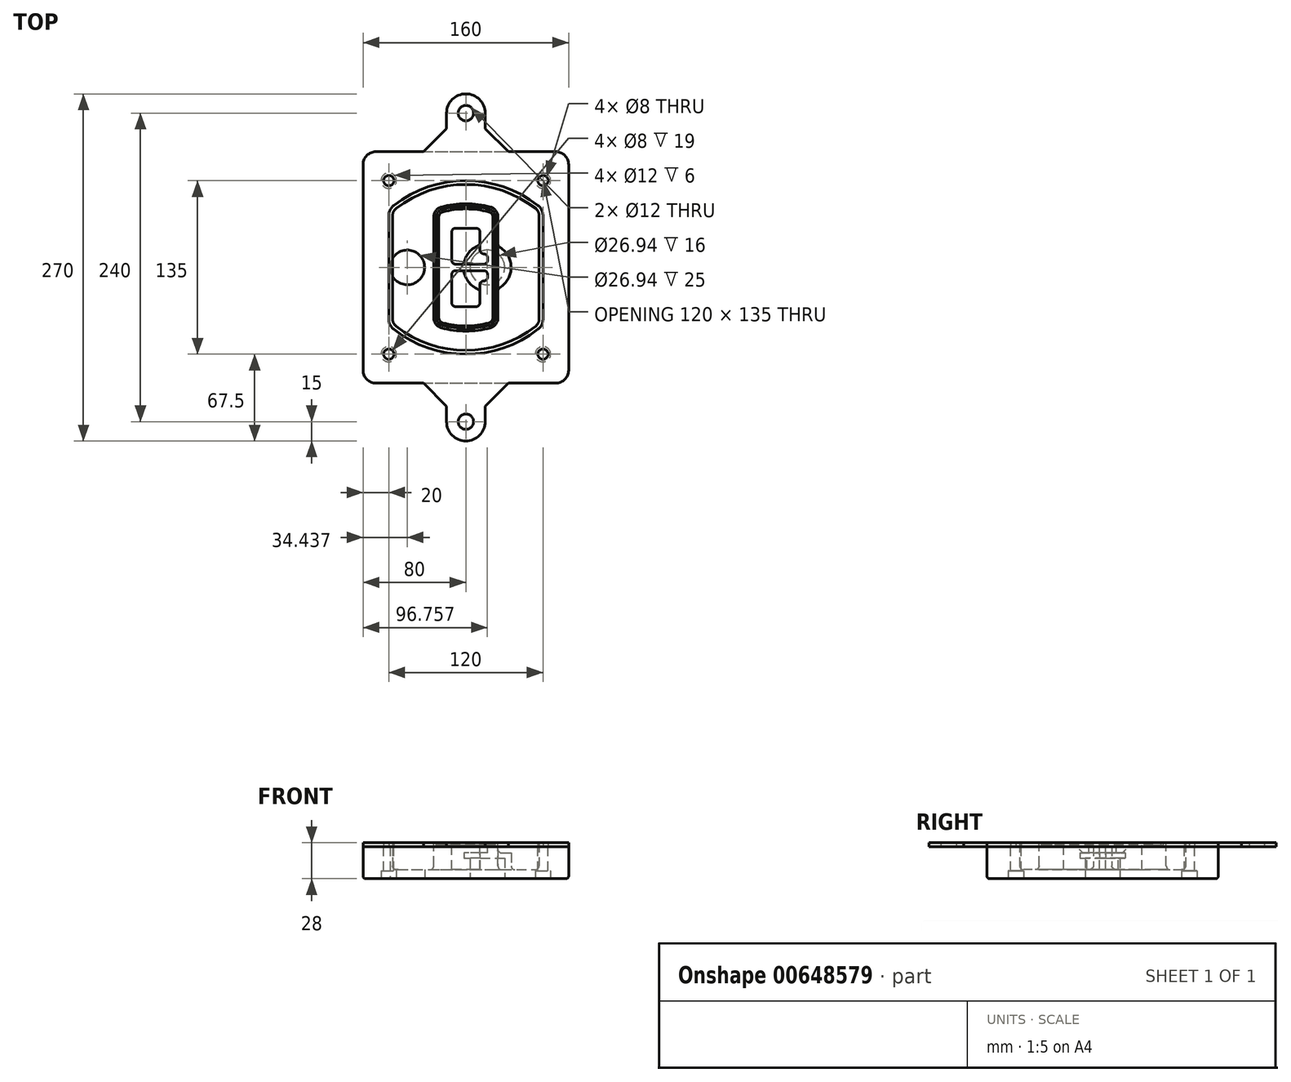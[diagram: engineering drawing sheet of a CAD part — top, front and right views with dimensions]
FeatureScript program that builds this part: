
annotation { "Feature Type Name" : "Feature", "Feature Type Description" : "" }
export const myFeature = defineFeature(function(context is Context, id is Id, definition is map)
    precondition{}
    {
        {
            var Q0;
            Q0=qCreatedBy(makeId("Top.planeOp"),FACE);
            var sketch = newSketch(context, id + "F0", { "sketchPlane" : qUnion([Q0])});
            skPoint(sketch, "E0.rect.middle", {"position": v(0, 0) * mm});
            skLineSegment(sketch, "E1.bottom", {"start": v(-70, -90) * mm, "end": v(70, -90) * mm});
            skLineSegment(sketch, "E1.top", {"start": v(-70, 90) * mm, "end": v(70, 90) * mm});
            skLineSegment(sketch, "E1.left", {"start": v(-80, -80) * mm, "end": v(-80, 80) * mm});
            skLineSegment(sketch, "E1.right", {"start": v(80, -80) * mm, "end": v(80, 80) * mm});
            skLineSegment(sketch, "E2", {"start": v(-80, 90) * mm, "end": v(80, -90) * mm, "construction": true});
            skLineSegment(sketch, "E3", {"start": v(80, 90) * mm, "end": v(-80, -90) * mm, "construction": true});
            skCircle(sketch, "E4", {"center": v(-60, 67.5) * mm, "radius": 4 * mm});
            skCircle(sketch, "E5", {"center": v(60, 67.5) * mm, "radius": 4 * mm});
            skCircle(sketch, "E6", {"center": v(60, -67.5) * mm, "radius": 4 * mm});
            skCircle(sketch, "E7", {"center": v(-60, -67.5) * mm, "radius": 4 * mm});
            skLineSegment(sketch, "E8", {"start": v(-60, 67.5) * mm, "end": v(60, 67.5) * mm, "construction": true});
            skLineSegment(sketch, "E9", {"start": v(60, 67.5) * mm, "end": v(60, -67.5) * mm, "construction": true});
            skLineSegment(sketch, "E10", {"start": v(60, -67.5) * mm, "end": v(-60, -67.5) * mm, "construction": true});
            skLineSegment(sketch, "E11", {"start": v(-60, -67.5) * mm, "end": v(-60, 67.5) * mm, "construction": true});
            skLineSegment(sketch, "E12", {"start": v(-60, 40.3) * mm, "end": v(-60, -40.3) * mm});
            skLineSegment(sketch, "E13", {"start": v(60, 40.3) * mm, "end": v(60, -40.3) * mm});
            skArc(sketch, "E14", {"start": v(56.15, 48.18) * mm, "mid": v(0, 67.5) * mm, "end": v(-56.15, 48.18) * mm});
            skArc(sketch, "E15", {"start": v(-56.15, -48.18) * mm, "mid": v(0, -67.5) * mm, "end": v(56.15, -48.18) * mm});
            skLineSegment(sketch, "E16", {"start": v(-60, 0) * mm, "end": v(60, 0) * mm, "construction": true});
            skPoint(sketch, "E17.visualSharp", {"position": v(-60, -45) * mm});
            skArc(sketch, "E17.filletArc", {"start": v(-60, -40.3) * mm, "mid": v(-58.99, -44.68) * mm, "end": v(-56.15, -48.18) * mm});
            skPoint(sketch, "E18.visualSharp", {"position": v(-60, 45) * mm});
            skArc(sketch, "E18.filletArc", {"start": v(-56.15, 48.18) * mm, "mid": v(-58.99, 44.68) * mm, "end": v(-60, 40.3) * mm});
            skPoint(sketch, "E19.visualSharp", {"position": v(60, 45) * mm});
            skArc(sketch, "E19.filletArc", {"start": v(60, 40.3) * mm, "mid": v(58.99, 44.68) * mm, "end": v(56.15, 48.18) * mm});
            skPoint(sketch, "E20.visualSharp", {"position": v(60, -45) * mm});
            skArc(sketch, "E20.filletArc", {"start": v(56.15, -48.18) * mm, "mid": v(58.99, -44.68) * mm, "end": v(60, -40.3) * mm});
            skPoint(sketch, "E21.visualSharp", {"position": v(-80, 90) * mm});
            skArc(sketch, "E21.filletArc", {"start": v(-70, 90) * mm, "mid": v(-77.07, 87.07) * mm, "end": v(-80, 80) * mm});
            skPoint(sketch, "E22.visualSharp", {"position": v(80, 90) * mm});
            skArc(sketch, "E22.filletArc", {"start": v(80, 80) * mm, "mid": v(77.07, 87.07) * mm, "end": v(70, 90) * mm});
            skPoint(sketch, "E23.visualSharp", {"position": v(80, -90) * mm});
            skArc(sketch, "E23.filletArc", {"start": v(70, -90) * mm, "mid": v(77.07, -87.07) * mm, "end": v(80, -80) * mm});
            skPoint(sketch, "E24.visualSharp", {"position": v(-80, -90) * mm});
            skArc(sketch, "E24.filletArc", {"start": v(-80, -80) * mm, "mid": v(-77.07, -87.07) * mm, "end": v(-70, -90) * mm});
            skArc(sketch, "E25.0", {"start": v(57, 40.3) * mm, "mid": v(56.3, 43.36) * mm, "end": v(54.3, 45.81) * mm});
            skLineSegment(sketch, "E25.1", {"start": v(57, 40.3) * mm, "end": v(57, -40.3) * mm});
            skArc(sketch, "E25.2", {"start": v(54.3, -45.81) * mm, "mid": v(56.3, -43.36) * mm, "end": v(57, -40.3) * mm});
            skArc(sketch, "E25.3", {"start": v(-54.3, -45.81) * mm, "mid": v(0, -64.5) * mm, "end": v(54.3, -45.81) * mm});
            skArc(sketch, "E25.4", {"start": v(-57, -40.3) * mm, "mid": v(-56.3, -43.36) * mm, "end": v(-54.3, -45.81) * mm});
            skArc(sketch, "E25.5", {"start": v(54.3, 45.81) * mm, "mid": v(0, 64.5) * mm, "end": v(-54.3, 45.81) * mm});
            skLineSegment(sketch, "E25.6", {"start": v(-57, 40.3) * mm, "end": v(-57, -40.3) * mm});
            skArc(sketch, "E25.7", {"start": v(-54.3, 45.81) * mm, "mid": v(-56.3, 43.36) * mm, "end": v(-57, 40.3) * mm});
            skArc(sketch, "E26.0", {"start": v(-58.62, 51.33) * mm, "mid": v(-62.58, 46.43) * mm, "end": v(-64, 40.3) * mm});
            skArc(sketch, "E26.1", {"start": v(58.62, 51.33) * mm, "mid": v(0, 71.5) * mm, "end": v(-58.62, 51.33) * mm});
            skArc(sketch, "E26.2", {"start": v(64, 40.3) * mm, "mid": v(62.58, 46.43) * mm, "end": v(58.62, 51.33) * mm});
            skLineSegment(sketch, "E26.3", {"start": v(64, 40.3) * mm, "end": v(64, -40.3) * mm});
            skArc(sketch, "E26.4", {"start": v(58.62, -51.33) * mm, "mid": v(62.58, -46.43) * mm, "end": v(64, -40.3) * mm});
            skLineSegment(sketch, "E26.5", {"start": v(-64, 40.3) * mm, "end": v(-64, -40.3) * mm});
            skArc(sketch, "E26.6", {"start": v(-58.62, -51.33) * mm, "mid": v(0, -71.5) * mm, "end": v(58.62, -51.33) * mm});
            skArc(sketch, "E26.7", {"start": v(-64, -40.3) * mm, "mid": v(-62.58, -46.43) * mm, "end": v(-58.62, -51.33) * mm});
            skSolve(sketch);
        }
        {
            var Q0;
            Q0=makeQuery(id+"F0.imprint","IMPRINT",FACE,{"disambiguationData":[TD([[makeQuery(id+"F0.imprint","IMPRINT",EDGE,{"derivedFrom":sQuery(id+"F0.wireOp",EDGE,"E1.bottom")}),1.0]])]});
            var Q1;
            Q1=makeQuery(id+"F0.imprint","IMPRINT",FACE,{"disambiguationData":[TD([[makeQuery(id+"F0.imprint","IMPRINT",EDGE,{"derivedFrom":sQuery(id+"F0.wireOp",EDGE,"E12")}),1.0]])]});
            var Q2;
            Q2=makeQuery(id+"F0.imprint","IMPRINT",FACE,{"disambiguationData":[TD([[makeQuery(id+"F0.imprint","IMPRINT",EDGE,{"derivedFrom":sQuery(id+"F0.wireOp",EDGE,"E25.0")}),1.0]])]});
            var Q3;
            Q3=makeQuery(id+"F0.imprint","IMPRINT",FACE,{"disambiguationData":[TD([[makeQuery(id+"F0.imprint","IMPRINT",EDGE,{"derivedFrom":sQuery(id+"F0.wireOp",EDGE,"E12")}),-1.0]])]});
            extrude(context, id + "F1", {"entities" : qUnion([Q0, Q1, Q2, Q3]), "oppositeDirection" : true, "depth" : 25 * mm});
        }
        {
            var Q0;
            Q0=makeQuery(id+"F0.imprint","IMPRINT",FACE,{"disambiguationData":[TD([[makeQuery(id+"F0.imprint","IMPRINT",EDGE,{"derivedFrom":sQuery(id+"F0.wireOp",EDGE,"E12")}),1.0]])]});
            extrude(context, id + "F2", {"entities" : qUnion([Q0]), "operationType" : NewBodyOperationType.ADD, "depth" : 3 * mm});
        }
        {
            var Q0;
            Q0=makeQuery(id+"F0.imprint","IMPRINT",FACE,{"disambiguationData":[TD([[makeQuery(id+"F0.imprint","IMPRINT",EDGE,{"derivedFrom":sQuery(id+"F0.wireOp",EDGE,"E25.0")}),1.0]])]});
            extrude(context, id + "F3", {"entities" : qUnion([Q0]), "operationType" : NewBodyOperationType.REMOVE, "oppositeDirection" : true, "depth" : 18 * mm});
        }
        {
            var Q0;
            Q0=makeQuery(id+"F2.opExtrude","CAP_FACE",FACE,{"disambiguationData":[OSD([sQuery(id+"F0.wireOp",EDGE,"E12"),sQuery(id+"F0.wireOp",EDGE,"E13"),sQuery(id+"F0.wireOp",EDGE,"E14"),sQuery(id+"F0.wireOp",EDGE,"E15"),sQuery(id+"F0.wireOp",EDGE,"E17.filletArc"),sQuery(id+"F0.wireOp",EDGE,"E18.filletArc"),sQuery(id+"F0.wireOp",EDGE,"E19.filletArc"),sQuery(id+"F0.wireOp",EDGE,"E20.filletArc"),sQuery(id+"F0.wireOp",EDGE,"E25.0"),sQuery(id+"F0.wireOp",EDGE,"E25.1"),sQuery(id+"F0.wireOp",EDGE,"E25.2"),sQuery(id+"F0.wireOp",EDGE,"E25.3"),sQuery(id+"F0.wireOp",EDGE,"E25.4"),sQuery(id+"F0.wireOp",EDGE,"E25.5"),sQuery(id+"F0.wireOp",EDGE,"E25.6"),sQuery(id+"F0.wireOp",EDGE,"E25.7")])],"isStart":false});
            var sketch = newSketch(context, id + "F4", { "sketchPlane" : qUnion([Q0])});
            skArc(sketch, "E27.0", {"start": v(-19.08, -46.97) * mm, "mid": v(0, -49.5) * mm, "end": v(19.08, -46.97) * mm});
            skArc(sketch, "E28.0", {"start": v(19.08, 46.97) * mm, "mid": v(0, 49.5) * mm, "end": v(-19.08, 46.97) * mm});
            skLineSegment(sketch, "E29", {"start": v(-25, 39.25) * mm, "end": v(-25, -39.25) * mm});
            skLineSegment(sketch, "E30", {"start": v(25, 39.25) * mm, "end": v(25, -39.25) * mm});
            skLineSegment(sketch, "E31", {"start": v(-25, 45.1) * mm, "end": v(25, 45.1) * mm, "construction": true});
            skLineSegment(sketch, "E32", {"start": v(-25, -45.1) * mm, "end": v(25, -45.1) * mm, "construction": true});
            skPoint(sketch, "E33.visualSharp", {"position": v(-25, 45.1) * mm});
            skArc(sketch, "E33.filletArc", {"start": v(-19.08, 46.97) * mm, "mid": v(-23.35, 44.11) * mm, "end": v(-25, 39.25) * mm});
            skPoint(sketch, "E34.visualSharp", {"position": v(25, 45.1) * mm});
            skArc(sketch, "E34.filletArc", {"start": v(25, 39.25) * mm, "mid": v(23.35, 44.11) * mm, "end": v(19.08, 46.97) * mm});
            skPoint(sketch, "E35.visualSharp", {"position": v(25, -45.1) * mm});
            skArc(sketch, "E35.filletArc", {"start": v(19.08, -46.97) * mm, "mid": v(23.35, -44.11) * mm, "end": v(25, -39.25) * mm});
            skPoint(sketch, "E36.visualSharp", {"position": v(-25, -45.1) * mm});
            skArc(sketch, "E36.filletArc", {"start": v(-25, -39.25) * mm, "mid": v(-23.35, -44.11) * mm, "end": v(-19.08, -46.97) * mm});
            skArc(sketch, "E37.0", {"start": v(54.3, 45.81) * mm, "mid": v(0, 64.5) * mm, "end": v(-54.3, 45.81) * mm});
            skArc(sketch, "E37.1", {"start": v(-54.3, 45.81) * mm, "mid": v(-56.3, 43.36) * mm, "end": v(-57, 40.3) * mm});
            skLineSegment(sketch, "E37.2", {"start": v(-57, 40.3) * mm, "end": v(-57, -40.3) * mm});
            skArc(sketch, "E37.3", {"start": v(-57, -40.3) * mm, "mid": v(-56.3, -43.36) * mm, "end": v(-54.3, -45.81) * mm});
            skArc(sketch, "E37.4", {"start": v(-54.3, -45.81) * mm, "mid": v(0, -64.5) * mm, "end": v(54.3, -45.81) * mm});
            skArc(sketch, "E37.5", {"start": v(54.3, -45.81) * mm, "mid": v(56.3, -43.36) * mm, "end": v(57, -40.3) * mm});
            skLineSegment(sketch, "E37.6", {"start": v(57, 40.3) * mm, "end": v(57, -40.3) * mm});
            skArc(sketch, "E37.7", {"start": v(57, 40.3) * mm, "mid": v(56.3, 43.36) * mm, "end": v(54.3, 45.81) * mm});
            skLineSegment(sketch, "E38.0", {"start": v(23, 39.25) * mm, "end": v(23, -39.25) * mm});
            skArc(sketch, "E38.1", {"start": v(18.56, -45.04) * mm, "mid": v(21.76, -42.9) * mm, "end": v(23, -39.25) * mm});
            skArc(sketch, "E38.2", {"start": v(-18.56, -45.04) * mm, "mid": v(0, -47.5) * mm, "end": v(18.56, -45.04) * mm});
            skArc(sketch, "E38.3", {"start": v(-23, -39.25) * mm, "mid": v(-21.76, -42.9) * mm, "end": v(-18.56, -45.04) * mm});
            skLineSegment(sketch, "E38.4", {"start": v(-23, 39.25) * mm, "end": v(-23, -39.25) * mm});
            skArc(sketch, "E38.5", {"start": v(23, 39.25) * mm, "mid": v(21.76, 42.9) * mm, "end": v(18.56, 45.04) * mm});
            skArc(sketch, "E38.6", {"start": v(-18.56, 45.04) * mm, "mid": v(-21.76, 42.9) * mm, "end": v(-23, 39.25) * mm});
            skArc(sketch, "E38.7", {"start": v(18.56, 45.04) * mm, "mid": v(0, 47.5) * mm, "end": v(-18.56, 45.04) * mm});
            skArc(sketch, "E39.0", {"start": v(21, 39.25) * mm, "mid": v(20.18, 41.68) * mm, "end": v(18.04, 43.1) * mm});
            skLineSegment(sketch, "E39.1", {"start": v(21, 39.25) * mm, "end": v(21, -39.25) * mm});
            skArc(sketch, "E39.2", {"start": v(18.04, -43.1) * mm, "mid": v(20.18, -41.68) * mm, "end": v(21, -39.25) * mm});
            skArc(sketch, "E39.3", {"start": v(-18.04, -43.1) * mm, "mid": v(0, -45.5) * mm, "end": v(18.04, -43.1) * mm});
            skArc(sketch, "E39.4", {"start": v(-21, -39.25) * mm, "mid": v(-20.18, -41.68) * mm, "end": v(-18.04, -43.1) * mm});
            skArc(sketch, "E39.5", {"start": v(18.04, 43.1) * mm, "mid": v(0, 45.5) * mm, "end": v(-18.04, 43.1) * mm});
            skLineSegment(sketch, "E39.6", {"start": v(-21, 39.25) * mm, "end": v(-21, -39.25) * mm});
            skArc(sketch, "E39.7", {"start": v(-18.04, 43.1) * mm, "mid": v(-20.18, 41.68) * mm, "end": v(-21, 39.25) * mm});
            skLineSegment(sketch, "E40", {"start": v(-25, 0) * mm, "end": v(25, 0) * mm, "construction": true});
            skLineSegment(sketch, "E41", {"start": v(-11, 5.5) * mm, "end": v(-11, 27.5) * mm});
            skLineSegment(sketch, "E42", {"start": v(-8, 30.5) * mm, "end": v(8, 30.5) * mm});
            skLineSegment(sketch, "E43", {"start": v(11, 27.5) * mm, "end": v(11, 13.5) * mm});
            skLineSegment(sketch, "E44", {"start": v(14, 10.5) * mm, "end": v(14, 10.5) * mm});
            skLineSegment(sketch, "E45", {"start": v(17, 7.5) * mm, "end": v(17, 5.5) * mm});
            skLineSegment(sketch, "E46", {"start": v(14, 2.5) * mm, "end": v(-8, 2.5) * mm});
            skPoint(sketch, "E47.visualSharp", {"position": v(-11, 30.5) * mm});
            skArc(sketch, "E47.filletArc", {"start": v(-8, 30.5) * mm, "mid": v(-10.12, 29.62) * mm, "end": v(-11, 27.5) * mm});
            skPoint(sketch, "E48.visualSharp", {"position": v(11, 30.5) * mm});
            skArc(sketch, "E48.filletArc", {"start": v(11, 27.5) * mm, "mid": v(10.12, 29.62) * mm, "end": v(8, 30.5) * mm});
            skPoint(sketch, "E49.visualSharp", {"position": v(11, 10.5) * mm});
            skArc(sketch, "E49.filletArc", {"start": v(11, 13.5) * mm, "mid": v(11.88, 11.38) * mm, "end": v(14, 10.5) * mm});
            skPoint(sketch, "E50.visualSharp", {"position": v(17, 10.5) * mm});
            skArc(sketch, "E50.filletArc", {"start": v(17, 7.5) * mm, "mid": v(16.12, 9.62) * mm, "end": v(14, 10.5) * mm});
            skPoint(sketch, "E51.visualSharp", {"position": v(17, 2.5) * mm});
            skArc(sketch, "E51.filletArc", {"start": v(14, 2.5) * mm, "mid": v(16.12, 3.38) * mm, "end": v(17, 5.5) * mm});
            skPoint(sketch, "E52.visualSharp", {"position": v(-11, 2.5) * mm});
            skArc(sketch, "E52.filletArc", {"start": v(-11, 5.5) * mm, "mid": v(-10.12, 3.38) * mm, "end": v(-8, 2.5) * mm});
            skLineSegment(sketch, "E53.0.MirrorCS", {"start": v(14, -2.5) * mm, "end": v(-8, -2.5) * mm});
            skArc(sketch, "E54.0.MirrorCS", {"start": v(-11, -5.5) * mm, "mid": v(-10.12, -3.38) * mm, "end": v(-8, -2.5) * mm});
            skLineSegment(sketch, "E55.0.MirrorCS", {"start": v(-11, -5.5) * mm, "end": v(-11, -27.5) * mm});
            skArc(sketch, "E56.0.MirrorCS", {"start": v(-8, -30.5) * mm, "mid": v(-10.12, -29.62) * mm, "end": v(-11, -27.5) * mm});
            skLineSegment(sketch, "E57.0.MirrorCS", {"start": v(-8, -30.5) * mm, "end": v(8, -30.5) * mm});
            skArc(sketch, "E58.0.MirrorCS", {"start": v(11, -27.5) * mm, "mid": v(10.12, -29.62) * mm, "end": v(8, -30.5) * mm});
            skLineSegment(sketch, "E59.0.MirrorCS", {"start": v(11, -27.5) * mm, "end": v(11, -13.5) * mm});
            skArc(sketch, "E60.0.MirrorCS", {"start": v(11, -13.5) * mm, "mid": v(11.88, -11.38) * mm, "end": v(14, -10.5) * mm});
            skArc(sketch, "E61.0.MirrorCS", {"start": v(17, -7.5) * mm, "mid": v(16.12, -9.62) * mm, "end": v(14, -10.5) * mm});
            skLineSegment(sketch, "E62.0.MirrorCS", {"start": v(17, -7.5) * mm, "end": v(17, -5.5) * mm});
            skArc(sketch, "E63.0.MirrorCS", {"start": v(14, -2.5) * mm, "mid": v(16.12, -3.38) * mm, "end": v(17, -5.5) * mm});
            skSolve(sketch);
        }
        {
            var Q0;
            Q0=makeQuery(id+"F4.imprint","IMPRINT",FACE,{"disambiguationData":[TD([[makeQuery(id+"F4.imprint","IMPRINT",EDGE,{"derivedFrom":sQuery(id+"F4.wireOp",EDGE,"E27.0")}),1.0]])]});
            var Q1;
            Q1=makeQuery(id+"F4.imprint","IMPRINT",FACE,{"disambiguationData":[TD([[makeQuery(id+"F4.imprint","IMPRINT",EDGE,{"derivedFrom":sQuery(id+"F4.wireOp",EDGE,"E38.0")}),-1.0]])]});
            var Q2;
            Q2=makeQuery(id+"F4.imprint","IMPRINT",FACE,{"disambiguationData":[TD([[makeQuery(id+"F4.imprint","IMPRINT",EDGE,{"derivedFrom":sQuery(id+"F4.wireOp",EDGE,"E39.0")}),1.0]])]});
            extrude(context, id + "F5", {"entities" : qUnion([Q0, Q1, Q2]), "operationType" : NewBodyOperationType.ADD, "endBound" : BoundingType.UP_TO_NEXT, "oppositeDirection" : true, "depth" : 25 * mm});
        }
        {
            var Q0;
            Q0=makeQuery(id+"F4.imprint","IMPRINT",FACE,{"disambiguationData":[TD([[makeQuery(id+"F4.imprint","IMPRINT",EDGE,{"derivedFrom":sQuery(id+"F4.wireOp",EDGE,"E38.0")}),-1.0]])]});
            extrude(context, id + "F6", {"entities" : qUnion([Q0]), "operationType" : NewBodyOperationType.REMOVE, "oppositeDirection" : true, "depth" : 2 * mm});
        }
        {
            var Q0;
            Q0=makeQuery(id+"F1.opExtrude","CAP_FACE",FACE,{"disambiguationData":[OSD([sQuery(id+"F0.wireOp",EDGE,"E1.bottom"),sQuery(id+"F0.wireOp",EDGE,"E1.top"),sQuery(id+"F0.wireOp",EDGE,"E1.left"),sQuery(id+"F0.wireOp",EDGE,"E1.right"),sQuery(id+"F0.wireOp",EDGE,"E4"),sQuery(id+"F0.wireOp",EDGE,"E5"),sQuery(id+"F0.wireOp",EDGE,"E6"),sQuery(id+"F0.wireOp",EDGE,"E7"),sQuery(id+"F0.wireOp",EDGE,"E21.filletArc"),sQuery(id+"F0.wireOp",EDGE,"E22.filletArc"),sQuery(id+"F0.wireOp",EDGE,"E23.filletArc"),sQuery(id+"F0.wireOp",EDGE,"E24.filletArc")])],"isStart":false});
            var sketch = newSketch(context, id + "F7", { "sketchPlane" : qUnion([Q0])});
            skCircle(sketch, "E64", {"center": v(16.76, 0) * mm, "radius": 13.47 * mm});
            skCircle(sketch, "E65", {"center": v(-45.56, 0) * mm, "radius": 13.47 * mm});
            skLineSegment(sketch, "E66", {"start": v(80, 0) * mm, "end": v(-80, 0) * mm});
            skCircle(sketch, "E67", {"center": v(16.76, 0) * mm, "radius": 18.47 * mm});
            skCircle(sketch, "E68", {"center": v(60, -67.5) * mm, "radius": 6 * mm});
            skCircle(sketch, "E69", {"center": v(-60, -67.5) * mm, "radius": 6 * mm});
            skCircle(sketch, "E70", {"center": v(-60, 67.5) * mm, "radius": 6 * mm});
            skCircle(sketch, "E71", {"center": v(60, 67.5) * mm, "radius": 6 * mm});
            skSolve(sketch);
        }
        {
            var Q0;
            {var subQ1=sQuery(id+"F7.wireOp",EDGE,"E66");var subQ4=sQuery(id+"F7.wireOp",EDGE,"E64");var subQ6=makeQuery(id+"F7.imprint","INTERSECT",VERTEX,{"disambiguationData":[OD(0.0)],"derivedFrom":[subQ4,subQ1]});Q0=makeQuery(id+"F7.imprint","IMPRINT",FACE,{"disambiguationData":[TD([[makeQuery(id+"F7.imprint","IMPRINT",EDGE,{"disambiguationData":[TD([[subQ6,-1.0]])],"derivedFrom":subQ4}),-1.0]])]});}
            var Q1;
            {var subQ0=sQuery(id+"F7.wireOp",EDGE,"E66");var subQ1=sQuery(id+"F7.wireOp",EDGE,"E64");var subQ3=makeQuery(id+"F7.imprint","INTERSECT",VERTEX,{"disambiguationData":[OD(0.0)],"derivedFrom":[subQ1,subQ0]});Q1=makeQuery(id+"F7.imprint","IMPRINT",FACE,{"disambiguationData":[TD([[makeQuery(id+"F7.imprint","IMPRINT",EDGE,{"disambiguationData":[TD([[subQ3,-1.0]])],"derivedFrom":subQ1}),1.0]])]});}
            var Q2;
            {var subQ0=sQuery(id+"F7.wireOp",EDGE,"E66");var subQ1=sQuery(id+"F7.wireOp",EDGE,"E64");var subQ3=makeQuery(id+"F7.imprint","INTERSECT",VERTEX,{"disambiguationData":[OD(0.0)],"derivedFrom":[subQ1,subQ0]});Q2=makeQuery(id+"F7.imprint","IMPRINT",FACE,{"disambiguationData":[TD([[makeQuery(id+"F7.imprint","IMPRINT",EDGE,{"disambiguationData":[TD([[subQ3,1.0]])],"derivedFrom":subQ1}),1.0]])]});}
            var Q3;
            {var subQ1=sQuery(id+"F7.wireOp",EDGE,"E66");var subQ4=sQuery(id+"F7.wireOp",EDGE,"E64");var subQ6=makeQuery(id+"F7.imprint","INTERSECT",VERTEX,{"disambiguationData":[OD(0.0)],"derivedFrom":[subQ4,subQ1]});Q3=makeQuery(id+"F7.imprint","IMPRINT",FACE,{"disambiguationData":[TD([[makeQuery(id+"F7.imprint","IMPRINT",EDGE,{"disambiguationData":[TD([[subQ6,1.0]])],"derivedFrom":subQ4}),-1.0]])]});}
            extrude(context, id + "F8", {"entities" : qUnion([Q0, Q1, Q2, Q3]), "operationType" : NewBodyOperationType.ADD, "oppositeDirection" : true, "depth" : 20 * mm});
        }
        {
            var Q0;
            {var subQ0=sQuery(id+"F7.wireOp",EDGE,"E66");var subQ1=sQuery(id+"F7.wireOp",EDGE,"E64");var subQ3=makeQuery(id+"F7.imprint","INTERSECT",VERTEX,{"disambiguationData":[OD(0.0)],"derivedFrom":[subQ1,subQ0]});Q0=makeQuery(id+"F7.imprint","IMPRINT",FACE,{"disambiguationData":[TD([[makeQuery(id+"F7.imprint","IMPRINT",EDGE,{"disambiguationData":[TD([[subQ3,-1.0]])],"derivedFrom":subQ1}),1.0]])]});}
            var Q1;
            {var subQ0=sQuery(id+"F7.wireOp",EDGE,"E66");var subQ1=sQuery(id+"F7.wireOp",EDGE,"E64");var subQ3=makeQuery(id+"F7.imprint","INTERSECT",VERTEX,{"disambiguationData":[OD(0.0)],"derivedFrom":[subQ1,subQ0]});Q1=makeQuery(id+"F7.imprint","IMPRINT",FACE,{"disambiguationData":[TD([[makeQuery(id+"F7.imprint","IMPRINT",EDGE,{"disambiguationData":[TD([[subQ3,1.0]])],"derivedFrom":subQ1}),1.0]])]});}
            extrude(context, id + "F9", {"entities" : qUnion([Q0, Q1]), "operationType" : NewBodyOperationType.REMOVE, "oppositeDirection" : true, "depth" : 16 * mm});
        }
        {
            var Q0;
            {var subQ0=sQuery(id+"F7.wireOp",EDGE,"E66");var subQ1=sQuery(id+"F7.wireOp",EDGE,"E65");var subQ3=makeQuery(id+"F7.imprint","INTERSECT",VERTEX,{"disambiguationData":[OD(0.0)],"derivedFrom":[subQ1,subQ0]});Q0=makeQuery(id+"F7.imprint","IMPRINT",FACE,{"disambiguationData":[TD([[makeQuery(id+"F7.imprint","IMPRINT",EDGE,{"disambiguationData":[TD([[subQ3,-1.0]])],"derivedFrom":subQ1}),1.0]])]});}
            var Q1;
            {var subQ0=sQuery(id+"F7.wireOp",EDGE,"E66");var subQ1=sQuery(id+"F7.wireOp",EDGE,"E65");var subQ3=makeQuery(id+"F7.imprint","INTERSECT",VERTEX,{"disambiguationData":[OD(0.0)],"derivedFrom":[subQ1,subQ0]});Q1=makeQuery(id+"F7.imprint","IMPRINT",FACE,{"disambiguationData":[TD([[makeQuery(id+"F7.imprint","IMPRINT",EDGE,{"disambiguationData":[TD([[subQ3,1.0]])],"derivedFrom":subQ1}),1.0]])]});}
            extrude(context, id + "F10", {"entities" : qUnion([Q0, Q1]), "operationType" : NewBodyOperationType.REMOVE, "oppositeDirection" : true, "depth" : 25 * mm});
        }
        {
            var Q0;
            Q0=makeQuery(id+"F7.imprint","IMPRINT",FACE,{"disambiguationData":[TD([[makeQuery(id+"F7.imprint","IMPRINT",EDGE,{"derivedFrom":sQuery(id+"F7.wireOp",EDGE,"E68")}),1.0]])]});
            var Q1;
            Q1=makeQuery(id+"F7.imprint","IMPRINT",FACE,{"disambiguationData":[TD([[makeQuery(id+"F7.imprint","IMPRINT",EDGE,{"derivedFrom":makeQuery(id+"F1.opExtrude","CAP_EDGE",EDGE,{"disambiguationData":[OSD([sQuery(id+"F0.wireOp",EDGE,"E5")])],"isStart":false})}),-1.0]])]});
            var Q2;
            Q2=makeQuery(id+"F7.imprint","IMPRINT",FACE,{"disambiguationData":[TD([[makeQuery(id+"F7.imprint","IMPRINT",EDGE,{"derivedFrom":sQuery(id+"F7.wireOp",EDGE,"E69")}),1.0]])]});
            var Q3;
            Q3=makeQuery(id+"F7.imprint","IMPRINT",FACE,{"disambiguationData":[TD([[makeQuery(id+"F7.imprint","IMPRINT",EDGE,{"derivedFrom":makeQuery(id+"F1.opExtrude","CAP_EDGE",EDGE,{"disambiguationData":[OSD([sQuery(id+"F0.wireOp",EDGE,"E4")])],"isStart":false})}),-1.0]])]});
            var Q4;
            Q4=makeQuery(id+"F7.imprint","IMPRINT",FACE,{"disambiguationData":[TD([[makeQuery(id+"F7.imprint","IMPRINT",EDGE,{"derivedFrom":sQuery(id+"F7.wireOp",EDGE,"E70")}),1.0]])]});
            var Q5;
            Q5=makeQuery(id+"F7.imprint","IMPRINT",FACE,{"disambiguationData":[TD([[makeQuery(id+"F7.imprint","IMPRINT",EDGE,{"derivedFrom":makeQuery(id+"F1.opExtrude","CAP_EDGE",EDGE,{"disambiguationData":[OSD([sQuery(id+"F0.wireOp",EDGE,"E7")])],"isStart":false})}),-1.0]])]});
            var Q6;
            Q6=makeQuery(id+"F7.imprint","IMPRINT",FACE,{"disambiguationData":[TD([[makeQuery(id+"F7.imprint","IMPRINT",EDGE,{"derivedFrom":sQuery(id+"F7.wireOp",EDGE,"E71")}),1.0]])]});
            var Q7;
            Q7=makeQuery(id+"F7.imprint","IMPRINT",FACE,{"disambiguationData":[TD([[makeQuery(id+"F7.imprint","IMPRINT",EDGE,{"derivedFrom":makeQuery(id+"F1.opExtrude","CAP_EDGE",EDGE,{"disambiguationData":[OSD([sQuery(id+"F0.wireOp",EDGE,"E6")])],"isStart":false})}),-1.0]])]});
            extrude(context, id + "F11", {"entities" : qUnion([Q0, Q1, Q2, Q3, Q4, Q5, Q6, Q7]), "operationType" : NewBodyOperationType.REMOVE, "oppositeDirection" : true, "depth" : 6 * mm});
        }
        {
            var Q0;
            Q0=makeQuery(id+"F9.boolean.opBoolean","COPY",FACE,{"derivedFrom":makeQuery(id+"F9.opExtrude","CAP_FACE",FACE,{"disambiguationData":[OSD([sQuery(id+"F7.wireOp",EDGE,"E64")])],"isStart":false})});
            var sketch = newSketch(context, id + "F12", { "sketchPlane" : qUnion([Q0])});
            skArc(sketch, "E72.0", {"start": v(11, 17.55) * mm, "mid": v(2.57, 11.82) * mm, "end": v(-1.54, 2.5) * mm});
            skArc(sketch, "E72.1", {"start": v(-1.54, -2.5) * mm, "mid": v(2.57, -11.82) * mm, "end": v(11, -17.55) * mm});
            skLineSegment(sketch, "E73", {"start": v(-1.54, -2.5) * mm, "end": v(14, -2.5) * mm});
            skLineSegment(sketch, "E74.0", {"start": v(14, 2.5) * mm, "end": v(-1.54, 2.5) * mm});
            skArc(sketch, "E74.1", {"start": v(14, 2.5) * mm, "mid": v(16.12, 3.38) * mm, "end": v(17, 5.5) * mm});
            skLineSegment(sketch, "E74.2", {"start": v(17, 7.5) * mm, "end": v(17, 5.5) * mm});
            skArc(sketch, "E74.3", {"start": v(17, 7.5) * mm, "mid": v(16.12, 9.62) * mm, "end": v(14, 10.5) * mm});
            skArc(sketch, "E74.4", {"start": v(11, 13.5) * mm, "mid": v(11.88, 11.38) * mm, "end": v(14, 10.5) * mm});
            skLineSegment(sketch, "E74.5", {"start": v(11, 17.55) * mm, "end": v(11, 13.5) * mm});
            skLineSegment(sketch, "E74.7", {"start": v(14, -2.5) * mm, "end": v(-1.54, -2.5) * mm});
            skArc(sketch, "E74.8", {"start": v(14, -2.5) * mm, "mid": v(16.12, -3.38) * mm, "end": v(17, -5.5) * mm});
            skLineSegment(sketch, "E74.9", {"start": v(17, -7.5) * mm, "end": v(17, -5.5) * mm});
            skArc(sketch, "E74.10", {"start": v(17, -7.5) * mm, "mid": v(16.12, -9.62) * mm, "end": v(14, -10.5) * mm});
            skArc(sketch, "E74.11", {"start": v(11, -13.5) * mm, "mid": v(11.88, -11.38) * mm, "end": v(14, -10.5) * mm});
            skLineSegment(sketch, "E74.12", {"start": v(11, -17.55) * mm, "end": v(11, -13.5) * mm});
            skPoint(sketch, "E75.orphan", {"position": v(11, -27.5) * mm});
            skPoint(sketch, "E76.orphan", {"position": v(-8, -2.5) * mm});
            skPoint(sketch, "E77.orphan", {"position": v(-8, 2.5) * mm});
            skPoint(sketch, "E78.orphan", {"position": v(11, 27.5) * mm});
            skSolve(sketch);
        }
        {
            var Q0;
            {var subQ7=sQuery(id+"F12.wireOp",EDGE,"E72.0");var subQ14=sQuery(id+"F12.wireOp",EDGE,"E72.1");var subQ16=sQuery(id+"F12.wireOp",EDGE,"E74.1");var subQ18=sQuery(id+"F12.wireOp",EDGE,"E74.8");Q0=qUnion([makeQuery(id+"F12.imprint","IMPRINT",FACE,{"disambiguationData":[TD([[makeQuery(id+"F12.imprint","IMPRINT",EDGE,{"derivedFrom":subQ7}),1.0]])]}),makeQuery(id+"F12.imprint","IMPRINT",FACE,{"disambiguationData":[TD([[makeQuery(id+"F12.imprint","IMPRINT",EDGE,{"derivedFrom":subQ14}),1.0]])]}),makeQuery(id+"F12.imprint","IMPRINT",FACE,{"disambiguationData":[TD([[makeQuery(id+"F12.imprint","IMPRINT",EDGE,{"derivedFrom":subQ16}),1.0]])]}),makeQuery(id+"F12.imprint","IMPRINT",FACE,{"disambiguationData":[TD([[makeQuery(id+"F12.imprint","IMPRINT",EDGE,{"derivedFrom":subQ18}),-1.0]])]})]);}
            var Q1;
            Q1=makeQuery(id+"F5.boolean.opBoolean","SPLIT",FACE,{"disambiguationData":[TD([makeQuery(id+"F5.opExtrude","SWEPT_FACE",FACE,{"disambiguationData":[OSD([sQuery(id+"F4.wireOp",EDGE,"E41")])]})])],"derivedFrom":makeQuery(id+"F3.boolean.opBoolean","COPY",FACE,{"derivedFrom":makeQuery(id+"F3.opExtrude","CAP_FACE",FACE,{"disambiguationData":[OSD([sQuery(id+"F0.wireOp",EDGE,"E25.0"),sQuery(id+"F0.wireOp",EDGE,"E25.1"),sQuery(id+"F0.wireOp",EDGE,"E25.2"),sQuery(id+"F0.wireOp",EDGE,"E25.3"),sQuery(id+"F0.wireOp",EDGE,"E25.4"),sQuery(id+"F0.wireOp",EDGE,"E25.5"),sQuery(id+"F0.wireOp",EDGE,"E25.6"),sQuery(id+"F0.wireOp",EDGE,"E25.7")])],"isStart":false})})});
            extrude(context, id + "F13", {"entities" : qUnion([Q0]), "operationType" : NewBodyOperationType.REMOVE, "endBound" : BoundingType.UP_TO_SURFACE, "endBoundEntityFace" : qUnion([Q1]), "depth" : 25 * mm});
        }
        {
            var Q0;
            Q0=makeQuery(id+"F3.boolean.opBoolean","COPY",EDGE,{"derivedFrom":makeQuery(id+"F3.opExtrude","CAP_EDGE",EDGE,{"disambiguationData":[OSD([sQuery(id+"F0.wireOp",EDGE,"E25.6")])],"isStart":false})});
            var Q1;
            Q1=makeQuery(id+"F8.boolean.opBoolean","INTERSECT",EDGE,{"derivedFrom":[makeQuery(id+"F5.opExtrude","SWEPT_FACE",FACE,{"disambiguationData":[OSD([sQuery(id+"F4.wireOp",EDGE,"E30")])]}),makeQuery(id+"F8.opExtrude","CAP_FACE",FACE,{"disambiguationData":[OSD([sQuery(id+"F7.wireOp",EDGE,"E67")])],"isStart":false})]});
            var Q2;
            Q2=makeQuery(id+"F8.boolean.opBoolean","INTERSECT",EDGE,{"disambiguationData":[OD(1.0)],"derivedFrom":[makeQuery(id+"F5.opExtrude","SWEPT_FACE",FACE,{"disambiguationData":[OSD([sQuery(id+"F4.wireOp",EDGE,"E30")])]}),makeQuery(id+"F8.opExtrude","SWEPT_FACE",FACE,{"disambiguationData":[OSD([sQuery(id+"F7.wireOp",EDGE,"E67")])]})]});
            var Q3;
            {var subQ0=sQuery(id+"F4.wireOp",EDGE,"E30");Q3=makeQuery(id+"F8.boolean.opBoolean","SPLIT",EDGE,{"disambiguationData":[TD([makeQuery(id+"F5.opExtrude","SWEPT_FACE",FACE,{"disambiguationData":[OSD([sQuery(id+"F4.wireOp",EDGE,"E35.filletArc")])]})])],"derivedFrom":makeQuery(id+"F5.opExtrude","CAP_EDGE",EDGE,{"disambiguationData":[OSD([subQ0])],"isStart":false})});}
            var Q4;
            {var subQ0=sQuery(id+"F0.wireOp",EDGE,"E25.7");var subQ1=sQuery(id+"F0.wireOp",EDGE,"E25.1");var subQ2=sQuery(id+"F0.wireOp",EDGE,"E25.6");var subQ3=sQuery(id+"F0.wireOp",EDGE,"E25.5");var subQ4=sQuery(id+"F0.wireOp",EDGE,"E25.4");var subQ5=sQuery(id+"F0.wireOp",EDGE,"E25.0");var subQ6=sQuery(id+"F0.wireOp",EDGE,"E25.2");var subQ7=sQuery(id+"F0.wireOp",EDGE,"E25.3");Q4=makeQuery(id+"F8.boolean.opBoolean","INTERSECT",EDGE,{"derivedFrom":[makeQuery(id+"F5.boolean.opBoolean","SPLIT",FACE,{"disambiguationData":[TD([makeQuery(id+"F2.opExtrude","SWEPT_FACE",FACE,{"disambiguationData":[OSD([subQ5])]})])],"derivedFrom":makeQuery(id+"F3.boolean.opBoolean","COPY",FACE,{"derivedFrom":makeQuery(id+"F3.opExtrude","CAP_FACE",FACE,{"disambiguationData":[OSD([subQ5,subQ1,subQ6,subQ7,subQ4,subQ3,subQ2,subQ0])],"isStart":false})})}),makeQuery(id+"F8.opExtrude","SWEPT_FACE",FACE,{"disambiguationData":[OSD([sQuery(id+"F7.wireOp",EDGE,"E67")])]})]});}
            var Q5;
            Q5=makeQuery(id+"F8.boolean.opBoolean","INTERSECT",EDGE,{"disambiguationData":[OD(0.0)],"derivedFrom":[makeQuery(id+"F5.opExtrude","SWEPT_FACE",FACE,{"disambiguationData":[OSD([sQuery(id+"F4.wireOp",EDGE,"E30")])]}),makeQuery(id+"F8.opExtrude","SWEPT_FACE",FACE,{"disambiguationData":[OSD([sQuery(id+"F7.wireOp",EDGE,"E67")])]})]});
            fillet(context, id + "F14", {"entities" : qUnion([Q0, Q1, Q2, Q3, Q4, Q5]), "radius" : 3 * mm, "tangentPropagation" : true, "allowEdgeOverflow" : false});
        }
        {
            var Q0;
            Q0=makeQuery(id+"F1.opExtrude","CAP_EDGE",EDGE,{"disambiguationData":[OSD([sQuery(id+"F0.wireOp",EDGE,"E1.bottom")])],"isStart":false});
            fillet(context, id + "F15", {"entities" : qUnion([Q0]), "radius" : 2 * mm, "tangentPropagation" : true, "allowEdgeOverflow" : false});
        }
        {
            var Q0;
            {var subQ0=sQuery(id+"F0.wireOp",EDGE,"E21.filletArc");var subQ1=sQuery(id+"F0.wireOp",EDGE,"E7");var subQ2=sQuery(id+"F0.wireOp",EDGE,"E6");var subQ3=sQuery(id+"F0.wireOp",EDGE,"E5");var subQ4=sQuery(id+"F0.wireOp",EDGE,"E4");var subQ5=sQuery(id+"F0.wireOp",EDGE,"E22.filletArc");var subQ6=sQuery(id+"F0.wireOp",EDGE,"E1.bottom");var subQ7=sQuery(id+"F0.wireOp",EDGE,"E1.right");var subQ8=sQuery(id+"F0.wireOp",EDGE,"E1.top");var subQ9=sQuery(id+"F0.wireOp",EDGE,"E1.left");var subQ10=sQuery(id+"F0.wireOp",EDGE,"E23.filletArc");var subQ11=sQuery(id+"F0.wireOp",EDGE,"E24.filletArc");Q0=makeQuery(id+"F2.boolean.opBoolean","SPLIT",FACE,{"disambiguationData":[TD([makeQuery(id+"F1.opExtrude","SWEPT_FACE",FACE,{"disambiguationData":[OSD([subQ6])]})])],"derivedFrom":makeQuery(id+"F1.opExtrude","CAP_FACE",FACE,{"disambiguationData":[OSD([subQ6,subQ8,subQ9,subQ7,subQ4,subQ3,subQ2,subQ1,subQ0,subQ5,subQ10,subQ11])],"isStart":true})});}
            var sketch = newSketch(context, id + "F16", { "sketchPlane" : qUnion([Q0])});
            skArc(sketch, "E79.0", {"start": v(-80, -80) * mm, "mid": v(-77.07, -87.07) * mm, "end": v(-70, -90) * mm});
            skLineSegment(sketch, "E79.1", {"start": v(-70, -90) * mm, "end": v(70, -90) * mm});
            skArc(sketch, "E79.2", {"start": v(70, -90) * mm, "mid": v(77.07, -87.07) * mm, "end": v(80, -80) * mm});
            skLineSegment(sketch, "E79.3", {"start": v(80, -80) * mm, "end": v(80, 80) * mm});
            skArc(sketch, "E79.4", {"start": v(80, 80) * mm, "mid": v(77.07, 87.07) * mm, "end": v(70, 90) * mm});
            skLineSegment(sketch, "E79.5", {"start": v(-70, 90) * mm, "end": v(70, 90) * mm});
            skArc(sketch, "E79.6", {"start": v(-70, 90) * mm, "mid": v(-77.07, 87.07) * mm, "end": v(-80, 80) * mm});
            skLineSegment(sketch, "E79.7", {"start": v(-80, -80) * mm, "end": v(-80, 80) * mm});
            skArc(sketch, "E79.8", {"start": v(-56.15, -48.18) * mm, "mid": v(0, -67.5) * mm, "end": v(56.15, -48.18) * mm});
            skArc(sketch, "E79.9", {"start": v(-60, -40.3) * mm, "mid": v(-58.99, -44.68) * mm, "end": v(-56.15, -48.18) * mm});
            skArc(sketch, "E79.10", {"start": v(56.15, -48.18) * mm, "mid": v(58.99, -44.68) * mm, "end": v(60, -40.3) * mm});
            skLineSegment(sketch, "E79.11", {"start": v(60, 40.3) * mm, "end": v(60, -40.3) * mm});
            skArc(sketch, "E79.12", {"start": v(60, 40.3) * mm, "mid": v(58.99, 44.68) * mm, "end": v(56.15, 48.18) * mm});
            skCircle(sketch, "E79.13", {"center": v(60, 67.5) * mm, "radius": 4 * mm});
            skCircle(sketch, "E79.14", {"center": v(60, -67.5) * mm, "radius": 4 * mm});
            skCircle(sketch, "E79.15", {"center": v(-60, -67.5) * mm, "radius": 4 * mm});
            skCircle(sketch, "E79.16", {"center": v(-60, 67.5) * mm, "radius": 4 * mm});
            skArc(sketch, "E79.17", {"start": v(56.15, 48.18) * mm, "mid": v(0, 67.5) * mm, "end": v(-56.15, 48.18) * mm});
            skArc(sketch, "E79.18", {"start": v(-56.15, 48.18) * mm, "mid": v(-58.99, 44.68) * mm, "end": v(-60, 40.3) * mm});
            skLineSegment(sketch, "E79.19", {"start": v(-60, 40.3) * mm, "end": v(-60, -40.3) * mm});
            skCircle(sketch, "E80", {"center": v(0, 120) * mm, "radius": 6 * mm});
            skArc(sketch, "E81", {"start": v(15, 120) * mm, "mid": v(0, 135) * mm, "end": v(-15, 120) * mm});
            skLineSegment(sketch, "E82", {"start": v(-15, 120) * mm, "end": v(-15, 108) * mm});
            skLineSegment(sketch, "E83", {"start": v(-15, 108) * mm, "end": v(-33, 90) * mm});
            skLineSegment(sketch, "E84", {"start": v(15, 120) * mm, "end": v(15, 108) * mm});
            skLineSegment(sketch, "E85", {"start": v(15, 108) * mm, "end": v(33, 90) * mm});
            skLineSegment(sketch, "E86", {"start": v(0, 130.78) * mm, "end": v(0, 90) * mm, "construction": true});
            skArc(sketch, "E87.MirrorCS", {"start": v(-15, 120) * mm, "mid": v(0, 135) * mm, "end": v(15, 120) * mm});
            skLineSegment(sketch, "E88", {"start": v(-103.38, 0) * mm, "end": v(100.18, 0) * mm, "construction": true});
            skLineSegment(sketch, "E89.MirrorCS", {"start": v(15, -120) * mm, "end": v(15, -108) * mm});
            skLineSegment(sketch, "E90.MirrorCS", {"start": v(-15, -120) * mm, "end": v(-15, -108) * mm});
            skCircle(sketch, "E91.MirrorC", {"center": v(0, -120) * mm, "radius": 6 * mm});
            skLineSegment(sketch, "E92.MirrorCS", {"start": v(15, -108) * mm, "end": v(33, -90) * mm});
            skArc(sketch, "E93.MirrorCS", {"start": v(15, -120) * mm, "mid": v(0, -135) * mm, "end": v(-15, -120) * mm});
            skLineSegment(sketch, "E94.MirrorCS", {"start": v(-15, -108) * mm, "end": v(-33, -90) * mm});
            skArc(sketch, "E95.MirrorCS", {"start": v(-15, -120) * mm, "mid": v(0, -135) * mm, "end": v(15, -120) * mm});
            skLineSegment(sketch, "E96.MirrorCS", {"start": v(0, -130.78) * mm, "end": v(0, -90) * mm, "construction": true});
            skSolve(sketch);
        }
        {
            var Q0;
            Q0 = qSketchRegion(id + "F16", true);
            var Q1;
            Q1=makeQuery(id+"F2.opExtrude","CAP_FACE",FACE,{"disambiguationData":[OSD([sQuery(id+"F0.wireOp",EDGE,"E12"),sQuery(id+"F0.wireOp",EDGE,"E13"),sQuery(id+"F0.wireOp",EDGE,"E14"),sQuery(id+"F0.wireOp",EDGE,"E15"),sQuery(id+"F0.wireOp",EDGE,"E17.filletArc"),sQuery(id+"F0.wireOp",EDGE,"E18.filletArc"),sQuery(id+"F0.wireOp",EDGE,"E19.filletArc"),sQuery(id+"F0.wireOp",EDGE,"E20.filletArc"),sQuery(id+"F0.wireOp",EDGE,"E25.0"),sQuery(id+"F0.wireOp",EDGE,"E25.1"),sQuery(id+"F0.wireOp",EDGE,"E25.2"),sQuery(id+"F0.wireOp",EDGE,"E25.3"),sQuery(id+"F0.wireOp",EDGE,"E25.4"),sQuery(id+"F0.wireOp",EDGE,"E25.5"),sQuery(id+"F0.wireOp",EDGE,"E25.6"),sQuery(id+"F0.wireOp",EDGE,"E25.7")])],"isStart":false});
            extrude(context, id + "F17", {"entities" : qUnion([Q0]), "endBound" : BoundingType.UP_TO_SURFACE, "depth" : 25 * mm, "endBoundEntityFace" : qUnion([Q1]), "offsetDistance" : 25 * mm});
        }
    });
